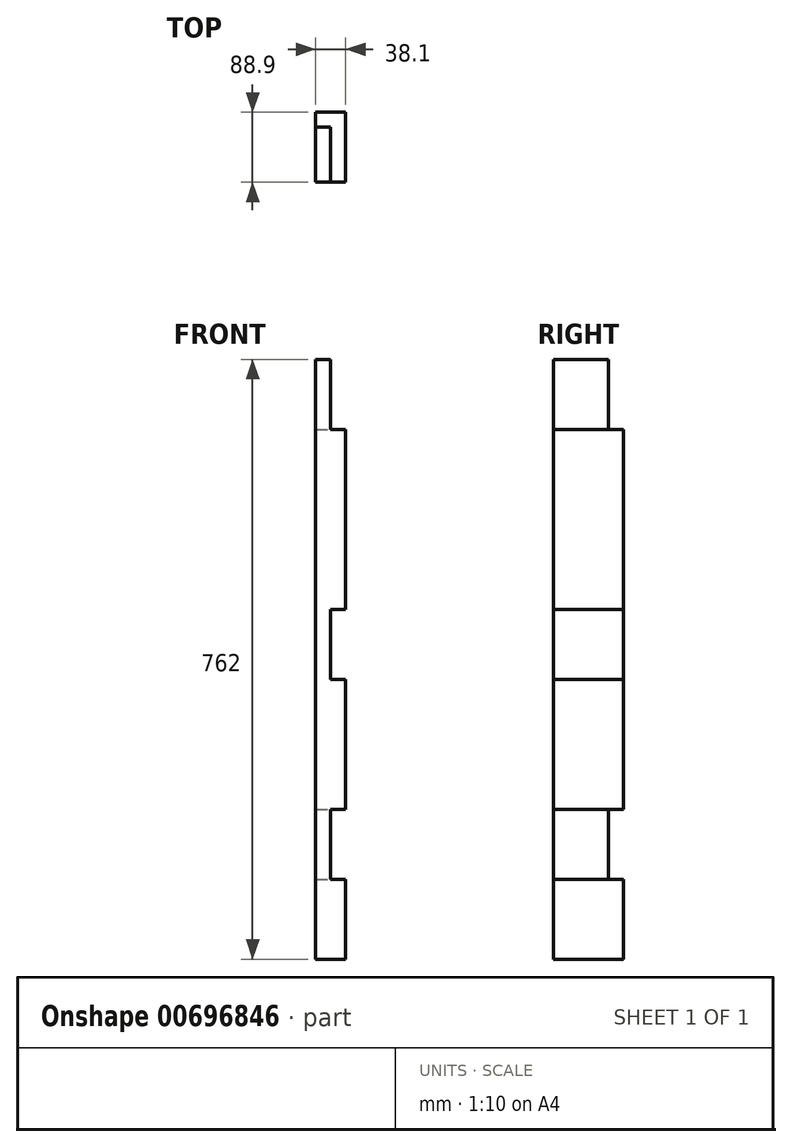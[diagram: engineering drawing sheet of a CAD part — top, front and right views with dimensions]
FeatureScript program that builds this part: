
annotation { "Feature Type Name" : "Feature", "Feature Type Description" : "" }
export const myFeature = defineFeature(function(context is Context, id is Id, definition is map)
    precondition{}
    {
        {
            var Q0;
            Q0=qCreatedBy(makeId("Top.planeOp"),FACE);
            var sketch = newSketch(context, id + "F0", { "sketchPlane" : qUnion([Q0])});
            skLineSegment(sketch, "E0.bottom", {"start": v(0, 0) * mm, "end": v(38.1, 0) * mm});
            skLineSegment(sketch, "E0.top", {"start": v(0, 88.9) * mm, "end": v(38.1, 88.9) * mm});
            skLineSegment(sketch, "E0.left", {"start": v(0, 0) * mm, "end": v(0, 88.9) * mm});
            skLineSegment(sketch, "E0.right", {"start": v(38.1, 0) * mm, "end": v(38.1, 88.9) * mm});
            skSolve(sketch);
        }
        {
            var Q0;
            Q0=qSketchRegion(id+"F0",true);
            extrude(context, id + "F1", {"entities" : qUnion([Q0]), "depth" : 762 * mm, "offsetDistance" : 25.4 * mm});
        }
        {
            var Q0;
            Q0=makeQuery(id+"F1.opExtrude","SWEPT_FACE",FACE,{"disambiguationData":[OSD([sQuery(id+"F0.wireOp",EDGE,"E0.bottom")])]});
            var sketch = newSketch(context, id + "F2", { "sketchPlane" : qUnion([Q0])});
            skLineSegment(sketch, "E1.bottom", {"start": v(38.1, 762) * mm, "end": v(19.05, 762) * mm});
            skLineSegment(sketch, "E1.top", {"start": v(38.1, 673.1) * mm, "end": v(19.05, 673.1) * mm});
            skLineSegment(sketch, "E1.left", {"start": v(38.1, 762) * mm, "end": v(38.1, 673.1) * mm});
            skLineSegment(sketch, "E1.right", {"start": v(19.05, 762) * mm, "end": v(19.05, 673.1) * mm});
            skSolve(sketch);
        }
        {
            var Q0;
            Q0=qSketchRegion(id+"F2",true);
            extrude(context, id + "F3", {"entities" : qUnion([Q0]), "operationType" : NewBodyOperationType.REMOVE, "endBound" : BoundingType.THROUGH_ALL, "oppositeDirection" : true, "depth" : 25.4 * mm, "offsetDistance" : 25.4 * mm});
        }
        {
            var Q0;
            Q0=makeQuery(id+"F1.opExtrude","SWEPT_FACE",FACE,{"disambiguationData":[OSD([sQuery(id+"F0.wireOp",EDGE,"E0.bottom")])]});
            var sketch = newSketch(context, id + "F4", { "sketchPlane" : qUnion([Q0])});
            skLineSegment(sketch, "E2.bottom", {"start": v(38.1, 190.5) * mm, "end": v(19.05, 190.5) * mm});
            skLineSegment(sketch, "E2.top", {"start": v(38.1, 101.6) * mm, "end": v(19.05, 101.6) * mm});
            skLineSegment(sketch, "E2.left", {"start": v(38.1, 190.5) * mm, "end": v(38.1, 101.6) * mm});
            skLineSegment(sketch, "E2.right", {"start": v(19.05, 190.5) * mm, "end": v(19.05, 101.6) * mm});
            skSolve(sketch);
        }
        {
            var Q0;
            Q0=qSketchRegion(id+"F4",true);
            extrude(context, id + "F5", {"entities" : qUnion([Q0]), "operationType" : NewBodyOperationType.REMOVE, "endBound" : BoundingType.THROUGH_ALL, "oppositeDirection" : true, "depth" : 25.4 * mm, "offsetDistance" : 25.4 * mm});
        }
        {
            var Q0;
            Q0=makeQuery(id+"F1.opExtrude","SWEPT_FACE",FACE,{"disambiguationData":[OSD([sQuery(id+"F0.wireOp",EDGE,"E0.bottom")])]});
            var sketch = newSketch(context, id + "F6", { "sketchPlane" : qUnion([Q0])});
            skLineSegment(sketch, "E3.bottom", {"start": v(38.1, 444.5) * mm, "end": v(19.05, 444.5) * mm});
            skLineSegment(sketch, "E3.top", {"start": v(38.1, 355.6) * mm, "end": v(19.05, 355.6) * mm});
            skLineSegment(sketch, "E3.left", {"start": v(38.1, 444.5) * mm, "end": v(38.1, 355.6) * mm});
            skLineSegment(sketch, "E3.right", {"start": v(19.05, 444.5) * mm, "end": v(19.05, 355.6) * mm});
            skSolve(sketch);
        }
        {
            var Q0;
            Q0=qSketchRegion(id+"F6",true);
            extrude(context, id + "F7", {"entities" : qUnion([Q0]), "operationType" : NewBodyOperationType.REMOVE, "endBound" : BoundingType.THROUGH_ALL, "oppositeDirection" : true, "depth" : 25.4 * mm, "offsetDistance" : 25.4 * mm});
        }
        {
            var Q0;
            Q0=makeQuery(id+"F3.boolean.opBoolean","COPY",FACE,{"derivedFrom":makeQuery(id+"F3.opExtrude","SWEPT_FACE",FACE,{"disambiguationData":[OSD([sQuery(id+"F2.wireOp",EDGE,"E1.right")])]})});
            var sketch = newSketch(context, id + "F8", { "sketchPlane" : qUnion([Q0])});
            skLineSegment(sketch, "E4.bottom", {"start": v(88.9, 673.1) * mm, "end": v(69.85, 673.1) * mm});
            skLineSegment(sketch, "E4.top", {"start": v(88.9, 762) * mm, "end": v(69.85, 762) * mm});
            skLineSegment(sketch, "E4.left", {"start": v(88.9, 673.1) * mm, "end": v(88.9, 762) * mm});
            skLineSegment(sketch, "E4.right", {"start": v(69.85, 673.1) * mm, "end": v(69.85, 762) * mm});
            skSolve(sketch);
        }
        {
            var Q0;
            Q0 = qSketchRegion(id + "F8", true);
            extrude(context, id + "F9", {"entities" : qUnion([Q0]), "operationType" : NewBodyOperationType.REMOVE, "endBound" : BoundingType.THROUGH_ALL, "oppositeDirection" : true, "depth" : 25.4 * mm, "offsetDistance" : 25.4 * mm});
        }
        {
            var Q0;
            Q0=makeQuery(id+"F5.boolean.opBoolean","COPY",FACE,{"derivedFrom":makeQuery(id+"F5.opExtrude","SWEPT_FACE",FACE,{"disambiguationData":[OSD([sQuery(id+"F4.wireOp",EDGE,"E2.right")])]})});
            var sketch = newSketch(context, id + "F10", { "sketchPlane" : qUnion([Q0])});
            skLineSegment(sketch, "E5.bottom", {"start": v(88.9, 190.5) * mm, "end": v(69.85, 190.5) * mm});
            skLineSegment(sketch, "E5.top", {"start": v(88.9, 101.6) * mm, "end": v(69.85, 101.6) * mm});
            skLineSegment(sketch, "E5.left", {"start": v(88.9, 190.5) * mm, "end": v(88.9, 101.6) * mm});
            skLineSegment(sketch, "E5.right", {"start": v(69.85, 190.5) * mm, "end": v(69.85, 101.6) * mm});
            skSolve(sketch);
        }
        {
            var Q0;
            Q0 = qSketchRegion(id + "F10", true);
            extrude(context, id + "F11", {"entities" : qUnion([Q0]), "operationType" : NewBodyOperationType.REMOVE, "endBound" : BoundingType.THROUGH_ALL, "oppositeDirection" : true, "depth" : 25.4 * mm, "offsetDistance" : 25.4 * mm});
        }
    });
